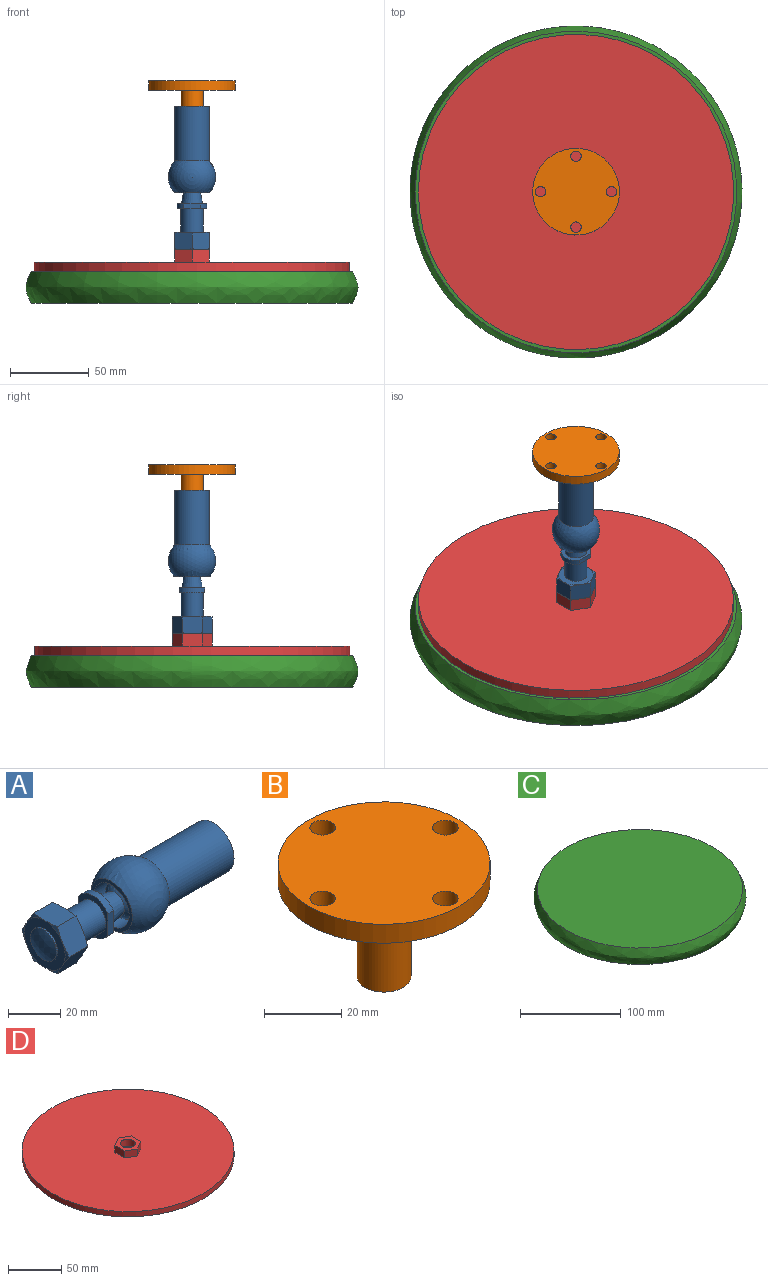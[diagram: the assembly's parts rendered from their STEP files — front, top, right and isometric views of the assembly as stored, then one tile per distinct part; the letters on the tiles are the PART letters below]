
ASSEMBLY  parts=4 mates=3
PART A: 39 faces, bbox 93x30x30 mm
  f0: sphere r=15mm, area 1903.7mm2, adj f1,f36
  f1: cylinder r=11mm len=34.8mm, axis (-1,0,0), area 2405.3mm2, adj f0,f38
  f2: cone r=6.59mm half-angle=45deg, axis (1,0,0), area 47.6mm2, adj f3,f38
  f3: cylinder r=6.19mm len=27.19mm, axis (-1,0,0), area 1057.1mm2, adj f2,f4
  f4: cone r=3.09mm half-angle=60deg, axis (1,0,0), area 138.9mm2, adj f3
  f5: cylinder r=9.5mm len=19mm, axis (-1,0,0), area 596.9mm2, adj f10,f36
  f6: sphere r=19.6mm, area 159.2mm2, adj f12
  f7: cylinder r=7mm len=15mm, axis (-1,0,0), area 659.7mm2, adj f31,f35
  f8: cylinder r=9.5mm len=16mm, axis (-1,0,0), area 57.1mm2, adj f33,f34,f35,f37
  f9: cone r=5.87mm half-angle=11deg, axis (-1,0,0), area 335.1mm2, adj f10,f37
  f10: sphere r=9.5mm, area 482.2mm2, adj f5,f9
  f11: cylinder r=9.5mm len=16mm, axis (-1,0,0), area 57.1mm2, adj f33,f34,f35,f37
  f12: cylinder r=7mm len=14mm, axis (-1,0,0), area 31.1mm2, adj f6,f32
  f13: plane 11x11mm, normal (0,-0.87,-0.5), area 135.7mm2, adj f15,f18,f21,f22,f25,f26
  f14: plane 11x11mm, normal (0,0.87,-0.5), area 135.7mm2, adj f15,f16,f23,f24,f29,f30
  f15: plane 12.7x11mm, normal (0,0,-1), area 135.7mm2, adj f13,f14,f22,f23,f25,f30
  f16: plane 11x11mm, normal (0,0.87,0.5), area 135.7mm2, adj f14,f17,f19,f24,f28,f29
  f17: plane 12.7x11mm, normal (0,0,1), area 135.7mm2, adj f16,f18,f19,f20,f27,f28
  f18: plane 11x11mm, normal (0,-0.87,0.5), area 135.7mm2, adj f13,f17,f20,f21,f26,f27
  f19: cone r=13.5mm half-angle=75deg, axis (-1,0,0), area 6.7mm2, adj f16,f17,f31
  f20: cone r=13.5mm half-angle=75deg, axis (-1,0,0), area 6.7mm2, adj f17,f18,f31
  f21: cone r=13.5mm half-angle=75deg, axis (-1,0,0), area 6.7mm2, adj f13,f18,f31
  f22: cone r=13.5mm half-angle=75deg, axis (-1,0,0), area 6.7mm2, adj f13,f15,f31
  f23: cone r=13.5mm half-angle=75deg, axis (-1,0,0), area 6.7mm2, adj f14,f15,f31
  f24: cone r=13.5mm half-angle=75deg, axis (-1,0,0), area 6.7mm2, adj f14,f16,f31
  f25: cone r=13.5mm half-angle=75deg, axis (1,0,0), area 6.7mm2, adj f13,f15,f32
  f26: cone r=13.5mm half-angle=75deg, axis (1,0,0), area 6.7mm2, adj f13,f18,f32
  f27: cone r=13.5mm half-angle=75deg, axis (1,0,0), area 6.7mm2, adj f17,f18,f32
  f28: cone r=13.5mm half-angle=75deg, axis (1,0,0), area 6.7mm2, adj f16,f17,f32
  f29: cone r=13.5mm half-angle=75deg, axis (1,0,0), area 6.7mm2, adj f14,f16,f32
  f30: cone r=13.5mm half-angle=75deg, axis (1,0,0), area 6.7mm2, adj f14,f15,f32
  f31: plane 22x22mm, normal (1,0,0), area 226.2mm2, adj f7,f19,f20,f21,f22,f23,f24
  f32: plane 22x22mm, normal (-1,0,0), area 226.2mm2, adj f12,f25,f26,f27,f28,f29,f30
  f33: plane 10.25x3mm, normal (0,-1,0), area 30.7mm2, adj f8,f11,f35,f37
  f34: plane 10.25x3mm, normal (0,1,0), area 30.7mm2, adj f8,f11,f35,f37
  f35: plane 19x16mm, normal (-1,0,0), area 108.7mm2, adj f7,f8,f11,f33,f34
  f36: plane 22.36x22.36mm, normal (-1,0,0), area 109.2mm2, adj f0,f5
  f37: plane 19x16mm, normal (1,0,0), area 120.2mm2, adj f8,f9,f11,f33,f34
  f38: plane 22x22mm, normal (1,0,0), area 226.2mm2, adj f1,f2
PART B: 9 faces, bbox 55x55x36 mm
  f0: cylinder r=27.5mm len=55mm, axis (0,0,-1), area 1036.7mm2, adj f1,f2
  f1: plane 55x55mm, normal (0,0,1), area 2239mm2, adj f0,f3,f4,f5,f6
  f2: plane 55x55mm, normal (0,0,-1), area 2085mm2, adj f0,f3,f4,f5,f6,f7
  f3: cylinder r=3.3mm len=6.6mm, axis (0,0,-1), area 124.4mm2, adj f1,f2
  f4: cylinder r=3.3mm len=6.6mm, axis (0,0,-1), area 124.4mm2, adj f1,f2
  f5: cylinder r=3.3mm len=6.6mm, axis (0,0,-1), area 124.4mm2, adj f1,f2
  f6: cylinder r=3.3mm len=6.6mm, axis (0,0,-1), area 124.4mm2, adj f1,f2
  f7: cylinder r=7mm len=30mm, axis (0,0,1), area 1319.5mm2, adj f2,f8
  f8: plane 14x14mm, normal (0,0,-1), area 153.9mm2, adj f7
PART C: 3 faces, bbox 210.7x210.7x20 mm
  f0: plane 204x204mm, normal (0,0,1), area 32685.1mm2, adj f1
  f1: revolved ~210.7x210.7mm, area 13917.6mm2, adj f0,f2
  f2: plane 204x204mm, normal (0,0,-1), area 32685.1mm2, adj f1
PART D: 12 faces, bbox 200x200x14 mm
  f0: plane 12.7x8mm, normal (1,0,0), area 101.6mm2, adj f1,f5,f7,f11
  f1: plane 11x8mm, normal (0.5,-0.87,0), area 101.6mm2, adj f0,f2,f7,f11
  f2: plane 11x8mm, normal (-0.5,-0.87,0), area 101.6mm2, adj f1,f3,f7,f11
  f3: plane 12.7x8mm, normal (-1,0,0), area 101.6mm2, adj f2,f4,f7,f11
  f4: plane 11x8mm, normal (-0.5,0.87,0), area 101.6mm2, adj f3,f5,f7,f11
  f5: plane 11x8mm, normal (0.5,0.87,0), area 101.6mm2, adj f0,f4,f7,f11
  f6: cylinder r=7mm len=14mm, axis (0,0,1), area 351.9mm2, adj f7,f8
  f7: plane 25.4x22mm, normal (0,0,1), area 265.2mm2, adj f0,f1,f2,f3,f4,f5,f6
  f8: plane 14x14mm, normal (0,0,1), area 153.9mm2, adj f6
  f9: cylinder r=100mm len=200mm, axis (0,0,1), area 3769.9mm2, adj f10,f11
  f10: plane 200x200mm, normal (0,0,-1), area 31415.9mm2, adj f9
  f11: plane 200x200mm, normal (0,0,1), area 30996.8mm2, adj f0,f1,f2,f3,f4,f5,f9
PLACE A rot(axis=(0,-1,0),90deg) t=(30.76,-30.7,-108.55)mm
PLACE B t=(30.76,-30.7,-53.55)mm
PLACE C t=(30.76,-30.7,-124.55)mm
PLACE D t=(30.76,-30.7,-124.55)mm
MATE fastened D.f6 <-> A.f1  axis (0,0,1) through (30.76,-30.7,-154.55)mm
MATE fastened C.f0 <-> D.f9  axis (0,0,1) through (30.76,-30.7,-168.55)mm
MATE fastened B.f7 <-> A.f1  axis (0,0,1) through (30.76,-30.7,-83.55)mm
